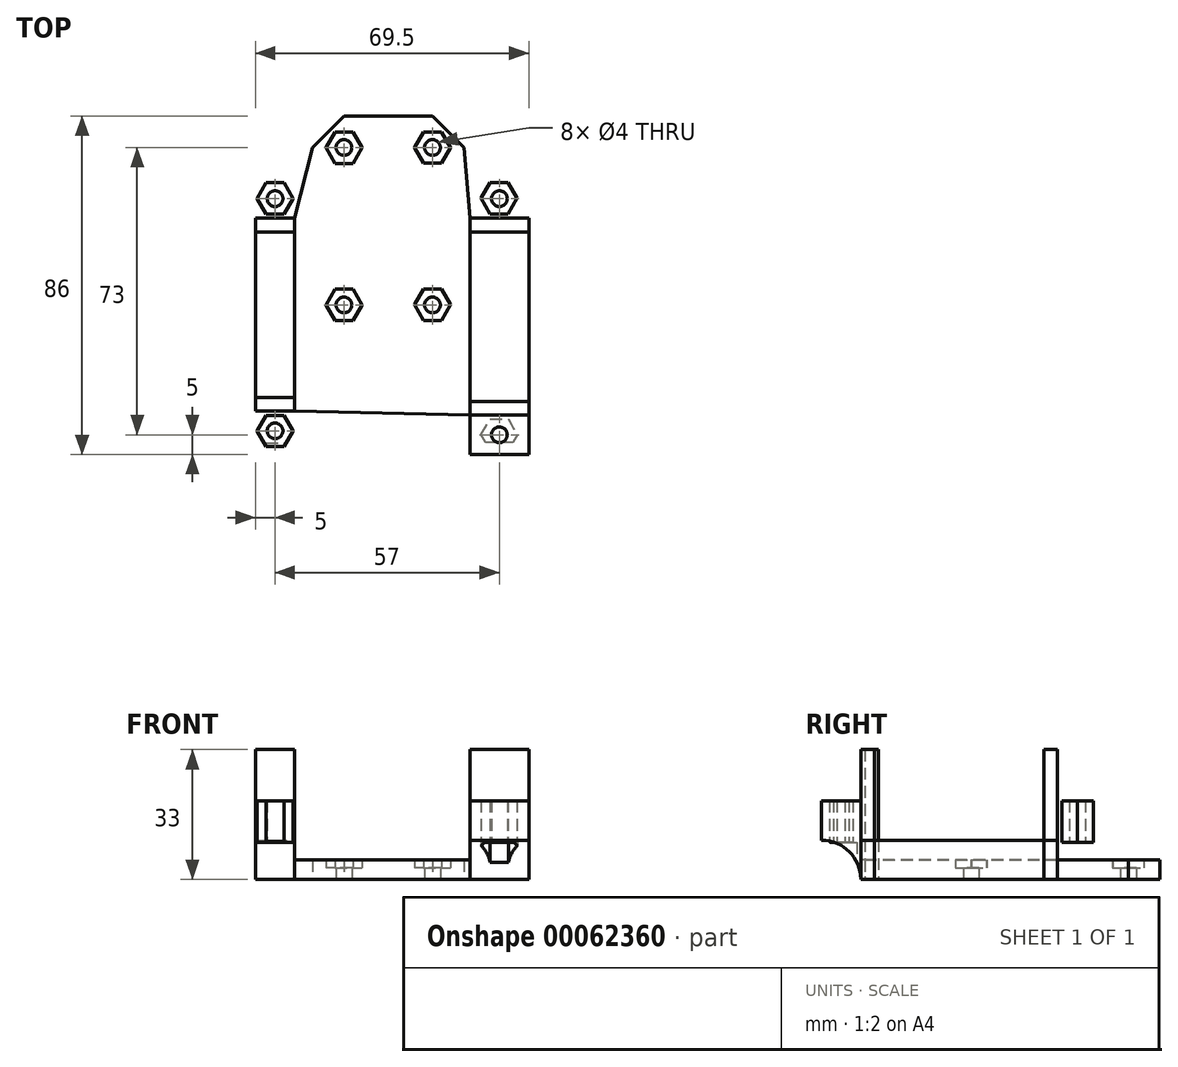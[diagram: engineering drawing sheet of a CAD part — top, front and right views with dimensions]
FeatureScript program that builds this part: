
annotation { "Feature Type Name" : "Feature", "Feature Type Description" : "" }
export const myFeature = defineFeature(function(context is Context, id is Id, definition is map)
    precondition{}
    {
        {
            var Q0;
            Q0=qCreatedBy(makeId("Top.planeOp"),FACE);
            var sketch = newSketch(context, id + "F0", { "sketchPlane" : qUnion([Q0])});
            skLineSegment(sketch, "E0.bottom", {"start": v(0, 0) * mm, "end": v(50.5, 0) * mm, "construction": true});
            skLineSegment(sketch, "E0.top", {"start": v(0, -69) * mm, "end": v(50.5, -69) * mm, "construction": true});
            skLineSegment(sketch, "E0.left", {"start": v(0, 0) * mm, "end": v(0, -69) * mm, "construction": true});
            skLineSegment(sketch, "E0.right", {"start": v(50.5, 0) * mm, "end": v(50.5, -69) * mm, "construction": true});
            skPoint(sketch, "E1", {"position": v(35.5, 8) * mm});
            skPoint(sketch, "E2", {"position": v(35.5, -32) * mm});
            skPoint(sketch, "E3", {"position": v(13, -32) * mm});
            skCircle(sketch, "E4", {"center": v(13, 8) * mm, "radius": 2 * mm});
            skCircle(sketch, "E5", {"center": v(35.5, 8) * mm, "radius": 2 * mm});
            skCircle(sketch, "E6", {"center": v(35.5, -32) * mm, "radius": 2 * mm});
            skCircle(sketch, "E7", {"center": v(13, -32) * mm, "radius": 2 * mm});
            skPoint(sketch, "E8", {"position": v(-9.5, 0) * mm});
            skPoint(sketch, "E9", {"position": v(60, 0) * mm});
            skPoint(sketch, "E10", {"position": v(45, 0) * mm});
            skPoint(sketch, "E11", {"position": v(0.5, 0) * mm});
            skPoint(sketch, "E12", {"position": v(60, -70) * mm});
            skPoint(sketch, "E13", {"position": v(-9.5, -69) * mm});
            skPoint(sketch, "E14", {"position": v(-9.5, -13.5) * mm});
            skPoint(sketch, "E15", {"position": v(-9.5, -55.5) * mm});
            skPoint(sketch, "E16", {"position": v(60, -13.5) * mm});
            skPoint(sketch, "E17", {"position": v(60, -56.5) * mm});
            skLineSegment(sketch, "E18.bottom", {"start": v(45, 0) * mm, "end": v(60, 0) * mm});
            skLineSegment(sketch, "E18.top", {"start": v(45, -70) * mm, "end": v(60, -70) * mm});
            skLineSegment(sketch, "E18.left", {"start": v(45, 0) * mm, "end": v(45, -70) * mm});
            skLineSegment(sketch, "E18.right", {"start": v(60, 0) * mm, "end": v(60, -70) * mm});
            skLineSegment(sketch, "E19.bottom", {"start": v(60, -13.5) * mm, "end": v(45, -13.5) * mm});
            skLineSegment(sketch, "E19.top", {"start": v(60, 0) * mm, "end": v(45, 0) * mm});
            skLineSegment(sketch, "E19.left", {"start": v(60, -13.5) * mm, "end": v(60, 0) * mm});
            skLineSegment(sketch, "E19.right", {"start": v(45, -13.5) * mm, "end": v(45, 0) * mm});
            skLineSegment(sketch, "E20.top", {"start": v(45, -56.5) * mm, "end": v(60, -56.5) * mm});
            skLineSegment(sketch, "E20.left", {"start": v(45, -70) * mm, "end": v(45, -56.5) * mm});
            skLineSegment(sketch, "E20.right", {"start": v(60, -70) * mm, "end": v(60, -56.5) * mm});
            skLineSegment(sketch, "E21.bottom", {"start": v(-9.5, -69) * mm, "end": v(0.5, -69) * mm});
            skLineSegment(sketch, "E21.top", {"start": v(-9.5, 0) * mm, "end": v(0.5, 0) * mm});
            skLineSegment(sketch, "E21.left", {"start": v(-9.5, -69) * mm, "end": v(-9.5, 0) * mm});
            skLineSegment(sketch, "E21.right", {"start": v(0.5, -69) * mm, "end": v(0.5, 0) * mm});
            skLineSegment(sketch, "E22.bottom", {"start": v(0.5, 0) * mm, "end": v(-9.5, 0) * mm});
            skLineSegment(sketch, "E22.top", {"start": v(0.5, -13.5) * mm, "end": v(-9.5, -13.5) * mm});
            skLineSegment(sketch, "E22.left", {"start": v(0.5, 0) * mm, "end": v(0.5, -13.5) * mm});
            skLineSegment(sketch, "E22.right", {"start": v(-9.5, 0) * mm, "end": v(-9.5, -13.5) * mm});
            skLineSegment(sketch, "E23.bottom", {"start": v(0.5, -69) * mm, "end": v(-9.5, -69) * mm});
            skLineSegment(sketch, "E23.top", {"start": v(0.5, -55.5) * mm, "end": v(-9.5, -55.5) * mm});
            skLineSegment(sketch, "E23.left", {"start": v(0.5, -69) * mm, "end": v(0.5, -55.5) * mm});
            skLineSegment(sketch, "E23.right", {"start": v(-9.5, -69) * mm, "end": v(-9.5, -55.5) * mm});
            skLineSegment(sketch, "E24", {"start": v(-9.5, -10) * mm, "end": v(0.5, -10) * mm});
            skLineSegment(sketch, "E25", {"start": v(-9.5, -59) * mm, "end": v(0.5, -59) * mm});
            skLineSegment(sketch, "E26", {"start": v(45, -60) * mm, "end": v(60, -60) * mm});
            skLineSegment(sketch, "E27", {"start": v(45, -10) * mm, "end": v(60, -10) * mm});
            skCircle(sketch, "E28", {"center": v(-4.5, -5) * mm, "radius": 2 * mm});
            skPoint(sketch, "E28.centerSnap0", {"position": v(-4.5, 0) * mm});
            skCircle(sketch, "E29", {"center": v(52.5, -5) * mm, "radius": 2 * mm});
            skPoint(sketch, "E29.centerSnap0", {"position": v(52.5, 0) * mm});
            skCircle(sketch, "E30", {"center": v(52.5, -65) * mm, "radius": 2 * mm});
            skPoint(sketch, "E30.centerSnap0", {"position": v(52.5, -70) * mm});
            skCircle(sketch, "E31", {"center": v(-4.5, -64) * mm, "radius": 2 * mm});
            skPoint(sketch, "E31.centerSnap0", {"position": v(-4.5, -69) * mm});
            skPoint(sketch, "E32", {"position": v(13, 16) * mm});
            skPoint(sketch, "E33", {"position": v(35.53, 16) * mm});
            skPoint(sketch, "E34", {"position": v(5, 8) * mm});
            skPoint(sketch, "E35", {"position": v(43.5, 8) * mm});
            skLineSegment(sketch, "E36", {"start": v(13, 16) * mm, "end": v(35.53, 16) * mm});
            skLineSegment(sketch, "E37", {"start": v(43.5, 8) * mm, "end": v(35.53, 16) * mm});
            skLineSegment(sketch, "E38", {"start": v(5, 8) * mm, "end": v(13, 16) * mm});
            skLineSegment(sketch, "E39", {"start": v(43.5, 8) * mm, "end": v(45, -10) * mm});
            skLineSegment(sketch, "E40", {"start": v(5, 8) * mm, "end": v(0.5, -10) * mm});
            skLineSegment(sketch, "E41", {"start": v(0.5, -59) * mm, "end": v(45, -60) * mm});
            skLineSegment(sketch, "E42", {"start": v(-58.4, 29.71) * mm, "end": v(-57.23, 30.88) * mm});
            skLineSegment(sketch, "E43", {"start": v(-57.23, 30.88) * mm, "end": v(-55.57, 30.88) * mm});
            skLineSegment(sketch, "E44", {"start": v(-55.57, 30.88) * mm, "end": v(-54.4, 29.71) * mm});
            skLineSegment(sketch, "E45", {"start": v(-54.4, 29.71) * mm, "end": v(-54.4, 28.05) * mm});
            skLineSegment(sketch, "E46", {"start": v(-54.4, 28.05) * mm, "end": v(-55.57, 26.88) * mm});
            skLineSegment(sketch, "E47", {"start": v(-55.57, 26.88) * mm, "end": v(-57.2, 26.88) * mm});
            skLineSegment(sketch, "E48", {"start": v(-57.2, 26.88) * mm, "end": v(-58.4, 28.03) * mm});
            skLineSegment(sketch, "E49", {"start": v(-58.4, 28.03) * mm, "end": v(-58.4, 29.71) * mm});
            skLineSegment(sketch, "E50.4", {"start": v(-64.18, 24.73) * mm, "end": v(-61.28, 24.73) * mm});
            skLineSegment(sketch, "E50.5", {"start": v(-61.28, 24.73) * mm, "end": v(-59.23, 22.67) * mm});
            skLineSegment(sketch, "E50.6", {"start": v(-59.23, 22.67) * mm, "end": v(-59.23, 19.78) * mm});
            skLineSegment(sketch, "E50.7", {"start": v(-59.23, 19.78) * mm, "end": v(-61.28, 17.73) * mm});
            skLineSegment(sketch, "E50.3", {"start": v(-61.28, 17.73) * mm, "end": v(-64.13, 17.73) * mm});
            skLineSegment(sketch, "E50.1", {"start": v(-64.13, 17.73) * mm, "end": v(-66.23, 19.73) * mm});
            skLineSegment(sketch, "E50.0", {"start": v(-66.23, 19.73) * mm, "end": v(-66.23, 22.67) * mm});
            skLineSegment(sketch, "E50.2", {"start": v(-66.23, 22.67) * mm, "end": v(-64.18, 24.73) * mm});
            skCircle(sketch, "E51.cCircle", {"center": v(-44.3, 30.36) * mm, "radius": 3.46 * mm, "construction": true});
            skLineSegment(sketch, "E51.0", {"start": v(-46.3, 33.82) * mm, "end": v(-42.3, 33.82) * mm});
            skLineSegment(sketch, "E51.1", {"start": v(-42.3, 33.82) * mm, "end": v(-40.3, 30.36) * mm});
            skLineSegment(sketch, "E51.2", {"start": v(-40.3, 30.36) * mm, "end": v(-42.3, 26.9) * mm});
            skLineSegment(sketch, "E51.3", {"start": v(-42.3, 26.9) * mm, "end": v(-46.3, 26.9) * mm});
            skLineSegment(sketch, "E51.4", {"start": v(-46.3, 26.9) * mm, "end": v(-48.3, 30.36) * mm});
            skLineSegment(sketch, "E51.5", {"start": v(-48.3, 30.36) * mm, "end": v(-46.3, 33.82) * mm});
            skPoint(sketch, "E51.0.midPoint", {"position": v(-44.3, 33.82) * mm});
            skLineSegment(sketch, "E52.0", {"start": v(-48.87, 30.36) * mm, "end": v(-46.58, 34.32) * mm});
            skLineSegment(sketch, "E52.1", {"start": v(-42, 34.32) * mm, "end": v(-39.71, 30.36) * mm});
            skLineSegment(sketch, "E52.2", {"start": v(-39.71, 30.36) * mm, "end": v(-42, 26.4) * mm});
            skLineSegment(sketch, "E52.3", {"start": v(-46.58, 34.32) * mm, "end": v(-42, 34.32) * mm});
            skLineSegment(sketch, "E52.4", {"start": v(-42, 26.4) * mm, "end": v(-46.58, 26.4) * mm});
            skLineSegment(sketch, "E52.5", {"start": v(-46.58, 26.4) * mm, "end": v(-48.87, 30.36) * mm});
            skLineSegment(sketch, "E53.0", {"start": v(8.46, -32) * mm, "end": v(10.75, -28.04) * mm});
            skLineSegment(sketch, "E53.3", {"start": v(10.75, -28.04) * mm, "end": v(15.33, -28.04) * mm});
            skLineSegment(sketch, "E53.1", {"start": v(15.33, -28.04) * mm, "end": v(17.62, -32) * mm});
            skLineSegment(sketch, "E53.2", {"start": v(17.62, -32) * mm, "end": v(15.33, -35.96) * mm});
            skLineSegment(sketch, "E53.4", {"start": v(15.33, -35.96) * mm, "end": v(10.75, -35.96) * mm});
            skLineSegment(sketch, "E53.5", {"start": v(10.75, -35.96) * mm, "end": v(8.46, -32) * mm});
            skLineSegment(sketch, "E54.0", {"start": v(30.94, -31.96) * mm, "end": v(33.23, -28) * mm});
            skLineSegment(sketch, "E54.3", {"start": v(33.23, -28) * mm, "end": v(37.8, -28) * mm});
            skLineSegment(sketch, "E54.1", {"start": v(37.8, -28) * mm, "end": v(40.1, -31.96) * mm});
            skLineSegment(sketch, "E54.2", {"start": v(40.1, -31.96) * mm, "end": v(37.8, -35.92) * mm});
            skLineSegment(sketch, "E54.4", {"start": v(37.8, -35.92) * mm, "end": v(33.23, -35.92) * mm});
            skLineSegment(sketch, "E54.5", {"start": v(33.23, -35.92) * mm, "end": v(30.94, -31.96) * mm});
            skLineSegment(sketch, "E55.0", {"start": v(8.41, 7.93) * mm, "end": v(10.7, 11.9) * mm});
            skLineSegment(sketch, "E55.3", {"start": v(10.7, 11.9) * mm, "end": v(15.28, 11.9) * mm});
            skLineSegment(sketch, "E55.1", {"start": v(15.28, 11.9) * mm, "end": v(17.57, 7.93) * mm});
            skLineSegment(sketch, "E55.2", {"start": v(17.57, 7.93) * mm, "end": v(15.28, 3.97) * mm});
            skLineSegment(sketch, "E55.4", {"start": v(15.28, 3.97) * mm, "end": v(10.7, 3.97) * mm});
            skLineSegment(sketch, "E55.5", {"start": v(10.7, 3.97) * mm, "end": v(8.41, 7.93) * mm});
            skLineSegment(sketch, "E56.0", {"start": v(30.95, 8) * mm, "end": v(33.24, 11.97) * mm});
            skLineSegment(sketch, "E56.3", {"start": v(33.24, 11.97) * mm, "end": v(37.82, 11.97) * mm});
            skLineSegment(sketch, "E56.1", {"start": v(37.82, 11.97) * mm, "end": v(40.1, 8) * mm});
            skLineSegment(sketch, "E56.2", {"start": v(40.1, 8) * mm, "end": v(37.82, 4.04) * mm});
            skLineSegment(sketch, "E56.4", {"start": v(37.82, 4.04) * mm, "end": v(33.24, 4.04) * mm});
            skLineSegment(sketch, "E56.5", {"start": v(33.24, 4.04) * mm, "end": v(30.95, 8) * mm});
            skLineSegment(sketch, "E57.0", {"start": v(-9.04, -64.04) * mm, "end": v(-6.75, -60.08) * mm});
            skLineSegment(sketch, "E57.3", {"start": v(-6.75, -60.08) * mm, "end": v(-2.18, -60.08) * mm});
            skLineSegment(sketch, "E57.1", {"start": v(-2.18, -60.08) * mm, "end": v(0.11, -64.04) * mm});
            skLineSegment(sketch, "E57.2", {"start": v(0.11, -64.04) * mm, "end": v(-2.18, -68) * mm});
            skLineSegment(sketch, "E57.4", {"start": v(-2.18, -68) * mm, "end": v(-6.75, -68) * mm});
            skLineSegment(sketch, "E57.5", {"start": v(-6.75, -68) * mm, "end": v(-9.04, -64.04) * mm});
            skLineSegment(sketch, "E58.0", {"start": v(47.87, -4.92) * mm, "end": v(50.16, -0.96) * mm});
            skLineSegment(sketch, "E58.3", {"start": v(50.16, -0.96) * mm, "end": v(54.73, -0.96) * mm});
            skLineSegment(sketch, "E58.1", {"start": v(54.73, -0.96) * mm, "end": v(57.02, -4.92) * mm});
            skLineSegment(sketch, "E58.2", {"start": v(57.02, -4.92) * mm, "end": v(54.73, -8.89) * mm});
            skLineSegment(sketch, "E58.4", {"start": v(54.73, -8.89) * mm, "end": v(50.16, -8.89) * mm});
            skLineSegment(sketch, "E58.5", {"start": v(50.16, -8.89) * mm, "end": v(47.87, -4.92) * mm});
            skLineSegment(sketch, "E59.0", {"start": v(-9.1, -4.94) * mm, "end": v(-6.8, -0.97) * mm});
            skLineSegment(sketch, "E59.3", {"start": v(-6.8, -0.97) * mm, "end": v(-2.23, -0.97) * mm});
            skLineSegment(sketch, "E59.1", {"start": v(-2.23, -0.97) * mm, "end": v(0.06, -4.94) * mm});
            skLineSegment(sketch, "E59.2", {"start": v(0.06, -4.94) * mm, "end": v(-2.23, -8.9) * mm});
            skLineSegment(sketch, "E59.4", {"start": v(-2.23, -8.9) * mm, "end": v(-6.8, -8.9) * mm});
            skLineSegment(sketch, "E59.5", {"start": v(-6.8, -8.9) * mm, "end": v(-9.1, -4.94) * mm});
            skLineSegment(sketch, "E60.0", {"start": v(47.88, -64.99) * mm, "end": v(50.17, -61.02) * mm});
            skLineSegment(sketch, "E60.3", {"start": v(50.17, -61.02) * mm, "end": v(54.75, -61.02) * mm});
            skLineSegment(sketch, "E60.1", {"start": v(54.75, -61.02) * mm, "end": v(57.04, -64.99) * mm});
            skLineSegment(sketch, "E60.2", {"start": v(57.04, -64.99) * mm, "end": v(54.75, -68.95) * mm});
            skLineSegment(sketch, "E60.4", {"start": v(54.75, -68.95) * mm, "end": v(50.17, -68.95) * mm});
            skLineSegment(sketch, "E60.5", {"start": v(50.17, -68.95) * mm, "end": v(47.88, -64.99) * mm});
            skSolve(sketch);
        }
        {
            var Q0;
            Q0=makeQuery(id+"F0.imprint","IMPRINT",FACE,{"disambiguationData":[TD([[makeQuery(id+"F0.imprint","IMPRINT",EDGE,{"derivedFrom":sQuery(id+"F0.wireOp",EDGE,"E18.left")}),1.0]])]});
            var Q1;
            Q1=makeQuery(id+"F0.imprint","IMPRINT",FACE,{"disambiguationData":[TD([[makeQuery(id+"F0.imprint","IMPRINT",EDGE,{"derivedFrom":sQuery(id+"F0.wireOp",EDGE,"E21.left")}),-1.0]])]});
            extrude(context, id + "F1", {"entities" : qUnion([Q0, Q1]), "depth" : 10 * mm});
        }
        {
            var Q0;
            {var subQ0=sQuery(id+"F0.wireOp",EDGE,"E23.top");Q0=makeQuery(id+"F0.imprint","IMPRINT",FACE,{"disambiguationData":[TD([[makeQuery(id+"F0.imprint","IMPRINT",EDGE,{"derivedFrom":subQ0}),1.0]])]});}
            var Q1;
            {var subQ0=sQuery(id+"F0.wireOp",EDGE,"E22.top");Q1=makeQuery(id+"F0.imprint","IMPRINT",FACE,{"disambiguationData":[TD([[makeQuery(id+"F0.imprint","IMPRINT",EDGE,{"derivedFrom":subQ0}),-1.0]])]});}
            var Q2;
            {var subQ0=sQuery(id+"F0.wireOp",EDGE,"E19.bottom");Q2=makeQuery(id+"F0.imprint","IMPRINT",FACE,{"disambiguationData":[TD([[makeQuery(id+"F0.imprint","IMPRINT",EDGE,{"derivedFrom":subQ0}),-1.0]])]});}
            var Q3;
            {var subQ0=sQuery(id+"F0.wireOp",EDGE,"E20.top");Q3=makeQuery(id+"F0.imprint","IMPRINT",FACE,{"disambiguationData":[TD([[makeQuery(id+"F0.imprint","IMPRINT",EDGE,{"derivedFrom":subQ0}),-1.0]])]});}
            extrude(context, id + "F2", {"entities" : qUnion([Q0, Q1, Q2, Q3]), "depth" : 33 * mm});
        }
        {
            var Q0;
            {var subQ1=sQuery(id+"F0.wireOp",EDGE,"E18.top");Q0=makeQuery(id+"F0.imprint","IMPRINT",FACE,{"disambiguationData":[TD([[makeQuery(id+"F0.imprint","IMPRINT",EDGE,{"derivedFrom":subQ1}),1.0]])]});}
            var Q1;
            Q1=makeQuery(id+"F0.imprint","IMPRINT",FACE,{"disambiguationData":[TD([[makeQuery(id+"F0.imprint","IMPRINT",EDGE,{"derivedFrom":sQuery(id+"F0.wireOp",EDGE,"E30")}),-1.0]])]});
            var Q2;
            {var subQ0=sQuery(id+"F0.wireOp",EDGE,"E23.bottom");Q2=makeQuery(id+"F0.imprint","IMPRINT",FACE,{"disambiguationData":[TD([[makeQuery(id+"F0.imprint","IMPRINT",EDGE,{"derivedFrom":subQ0}),-1.0]])]});}
            var Q3;
            Q3=makeQuery(id+"F0.imprint","IMPRINT",FACE,{"disambiguationData":[TD([[makeQuery(id+"F0.imprint","IMPRINT",EDGE,{"derivedFrom":sQuery(id+"F0.wireOp",EDGE,"E31")}),-1.0]])]});
            var Q4;
            Q4=makeQuery(id+"F0.imprint","IMPRINT",FACE,{"disambiguationData":[TD([[makeQuery(id+"F0.imprint","IMPRINT",EDGE,{"derivedFrom":sQuery(id+"F0.wireOp",EDGE,"E28")}),-1.0]])]});
            var Q5;
            {var subQ1=sQuery(id+"F0.wireOp",EDGE,"E22.bottom");Q5=makeQuery(id+"F0.imprint","IMPRINT",FACE,{"disambiguationData":[TD([[makeQuery(id+"F0.imprint","IMPRINT",EDGE,{"derivedFrom":subQ1}),1.0]])]});}
            var Q6;
            Q6=makeQuery(id+"F0.imprint","IMPRINT",FACE,{"disambiguationData":[TD([[makeQuery(id+"F0.imprint","IMPRINT",EDGE,{"derivedFrom":sQuery(id+"F0.wireOp",EDGE,"E29")}),-1.0]])]});
            var Q7;
            {var subQ1=sQuery(id+"F0.wireOp",EDGE,"E19.top");Q7=makeQuery(id+"F0.imprint","IMPRINT",FACE,{"disambiguationData":[TD([[makeQuery(id+"F0.imprint","IMPRINT",EDGE,{"derivedFrom":subQ1}),1.0]])]});}
            extrude(context, id + "F3", {"entities" : qUnion([Q0, Q1, Q2, Q3, Q4, Q5, Q6, Q7]), "depth" : 20 * mm});
        }
        {
            var Q0;
            Q0=makeQuery(id+"F0.imprint","IMPRINT",FACE,{"disambiguationData":[TD([[makeQuery(id+"F0.imprint","IMPRINT",EDGE,{"derivedFrom":sQuery(id+"F0.wireOp",EDGE,"E30")}),-1.0]])]});
            var Q1;
            Q1=makeQuery(id+"F0.imprint","IMPRINT",FACE,{"disambiguationData":[TD([[makeQuery(id+"F0.imprint","IMPRINT",EDGE,{"derivedFrom":sQuery(id+"F0.wireOp",EDGE,"E29")}),-1.0]])]});
            var Q2;
            Q2=makeQuery(id+"F0.imprint","IMPRINT",FACE,{"disambiguationData":[TD([[makeQuery(id+"F0.imprint","IMPRINT",EDGE,{"derivedFrom":sQuery(id+"F0.wireOp",EDGE,"E31")}),-1.0]])]});
            var Q3;
            Q3=makeQuery(id+"F0.imprint","IMPRINT",FACE,{"disambiguationData":[TD([[makeQuery(id+"F0.imprint","IMPRINT",EDGE,{"derivedFrom":sQuery(id+"F0.wireOp",EDGE,"E28")}),-1.0]])]});
            extrude(context, id + "F4", {"entities" : qUnion([Q0, Q1, Q2, Q3]), "operationType" : NewBodyOperationType.REMOVE, "depth" : 9.5 * mm});
        }
        {
            var Q0;
            {var subQ1=sQuery(id+"F0.wireOp",EDGE,"E18.top");Q0=makeQuery(id+"F0.imprint","IMPRINT",FACE,{"disambiguationData":[TD([[makeQuery(id+"F0.imprint","IMPRINT",EDGE,{"derivedFrom":subQ1}),1.0]])]});}
            var Q1;
            Q1=makeQuery(id+"F0.imprint","IMPRINT",FACE,{"disambiguationData":[TD([[makeQuery(id+"F0.imprint","IMPRINT",EDGE,{"derivedFrom":sQuery(id+"F0.wireOp",EDGE,"E30")}),-1.0]])]});
            var Q2;
            Q2=makeQuery(id+"F0.imprint","IMPRINT",FACE,{"disambiguationData":[TD([[makeQuery(id+"F0.imprint","IMPRINT",EDGE,{"derivedFrom":sQuery(id+"F0.wireOp",EDGE,"E30")}),1.0]])]});
            var Q3;
            {var subQ0=sQuery(id+"F0.wireOp",EDGE,"E23.bottom");Q3=makeQuery(id+"F0.imprint","IMPRINT",FACE,{"disambiguationData":[TD([[makeQuery(id+"F0.imprint","IMPRINT",EDGE,{"derivedFrom":subQ0}),-1.0]])]});}
            var Q4;
            Q4=makeQuery(id+"F0.imprint","IMPRINT",FACE,{"disambiguationData":[TD([[makeQuery(id+"F0.imprint","IMPRINT",EDGE,{"derivedFrom":sQuery(id+"F0.wireOp",EDGE,"E31")}),-1.0]])]});
            var Q5;
            Q5=makeQuery(id+"F0.imprint","IMPRINT",FACE,{"disambiguationData":[TD([[makeQuery(id+"F0.imprint","IMPRINT",EDGE,{"derivedFrom":sQuery(id+"F0.wireOp",EDGE,"E31")}),1.0]])]});
            var Q6;
            Q6=sQuery(id+"F0.wireOp",EDGE,"E18.top");
            revolve(context, id + "F5", {"operationType" : NewBodyOperationType.REMOVE, "entities" : qUnion([Q0, Q1, Q2, Q3, Q4, Q5]), "axis" : qUnion([Q6]), "revolveType" : RevolveType.FULL, "oppositeDirection" : true});
        }
        {
            var Q0;
            {var subQ1=sQuery(id+"F0.wireOp",EDGE,"E19.top");Q0=makeQuery(id+"F0.imprint","IMPRINT",FACE,{"disambiguationData":[TD([[makeQuery(id+"F0.imprint","IMPRINT",EDGE,{"derivedFrom":subQ1}),1.0]])]});}
            var Q1;
            Q1=makeQuery(id+"F0.imprint","IMPRINT",FACE,{"disambiguationData":[TD([[makeQuery(id+"F0.imprint","IMPRINT",EDGE,{"derivedFrom":sQuery(id+"F0.wireOp",EDGE,"E29")}),-1.0]])]});
            var Q2;
            Q2=makeQuery(id+"F0.imprint","IMPRINT",FACE,{"disambiguationData":[TD([[makeQuery(id+"F0.imprint","IMPRINT",EDGE,{"derivedFrom":sQuery(id+"F0.wireOp",EDGE,"E29")}),1.0]])]});
            var Q3;
            {var subQ1=sQuery(id+"F0.wireOp",EDGE,"E22.bottom");Q3=makeQuery(id+"F0.imprint","IMPRINT",FACE,{"disambiguationData":[TD([[makeQuery(id+"F0.imprint","IMPRINT",EDGE,{"derivedFrom":subQ1}),1.0]])]});}
            var Q4;
            Q4=makeQuery(id+"F0.imprint","IMPRINT",FACE,{"disambiguationData":[TD([[makeQuery(id+"F0.imprint","IMPRINT",EDGE,{"derivedFrom":sQuery(id+"F0.wireOp",EDGE,"E28")}),-1.0]])]});
            var Q5;
            Q5=makeQuery(id+"F0.imprint","IMPRINT",FACE,{"disambiguationData":[TD([[makeQuery(id+"F0.imprint","IMPRINT",EDGE,{"derivedFrom":sQuery(id+"F0.wireOp",EDGE,"E28")}),1.0]])]});
            var Q6;
            Q6=sQuery(id+"F0.wireOp",EDGE,"E18.bottom");
            revolve(context, id + "F6", {"operationType" : NewBodyOperationType.REMOVE, "entities" : qUnion([Q0, Q1, Q2, Q3, Q4, Q5]), "axis" : qUnion([Q6]), "revolveType" : RevolveType.FULL, "oppositeDirection" : true});
        }
        {
            var Q0;
            {var subQ1=sQuery(id+"F0.wireOp",EDGE,"E18.left");Q0=makeQuery(id+"F0.imprint","IMPRINT",FACE,{"disambiguationData":[TD([[makeQuery(id+"F0.imprint","IMPRINT",EDGE,{"derivedFrom":subQ1}),-1.0]])]});}
            extrude(context, id + "F7", {"entities" : qUnion([Q0]), "depth" : 5 * mm});
        }
        {
            var Q0;
            Q0=makeQuery(id+"F0.imprint","IMPRINT",FACE,{"disambiguationData":[TD([[makeQuery(id+"F0.imprint","IMPRINT",EDGE,{"derivedFrom":sQuery(id+"F0.wireOp",EDGE,"E7")}),-1.0]])]});
            var Q1;
            Q1=makeQuery(id+"F0.imprint","IMPRINT",FACE,{"disambiguationData":[TD([[makeQuery(id+"F0.imprint","IMPRINT",EDGE,{"derivedFrom":sQuery(id+"F0.wireOp",EDGE,"E6")}),-1.0]])]});
            var Q2;
            Q2=makeQuery(id+"F0.imprint","IMPRINT",FACE,{"disambiguationData":[TD([[makeQuery(id+"F0.imprint","IMPRINT",EDGE,{"derivedFrom":sQuery(id+"F0.wireOp",EDGE,"E5")}),-1.0]])]});
            var Q3;
            Q3=makeQuery(id+"F0.imprint","IMPRINT",FACE,{"disambiguationData":[TD([[makeQuery(id+"F0.imprint","IMPRINT",EDGE,{"derivedFrom":sQuery(id+"F0.wireOp",EDGE,"E4")}),-1.0]])]});
            extrude(context, id + "F8", {"entities" : qUnion([Q0, Q1, Q2, Q3]), "operationType" : NewBodyOperationType.ADD, "depth" : 3 * mm});
        }
    });
